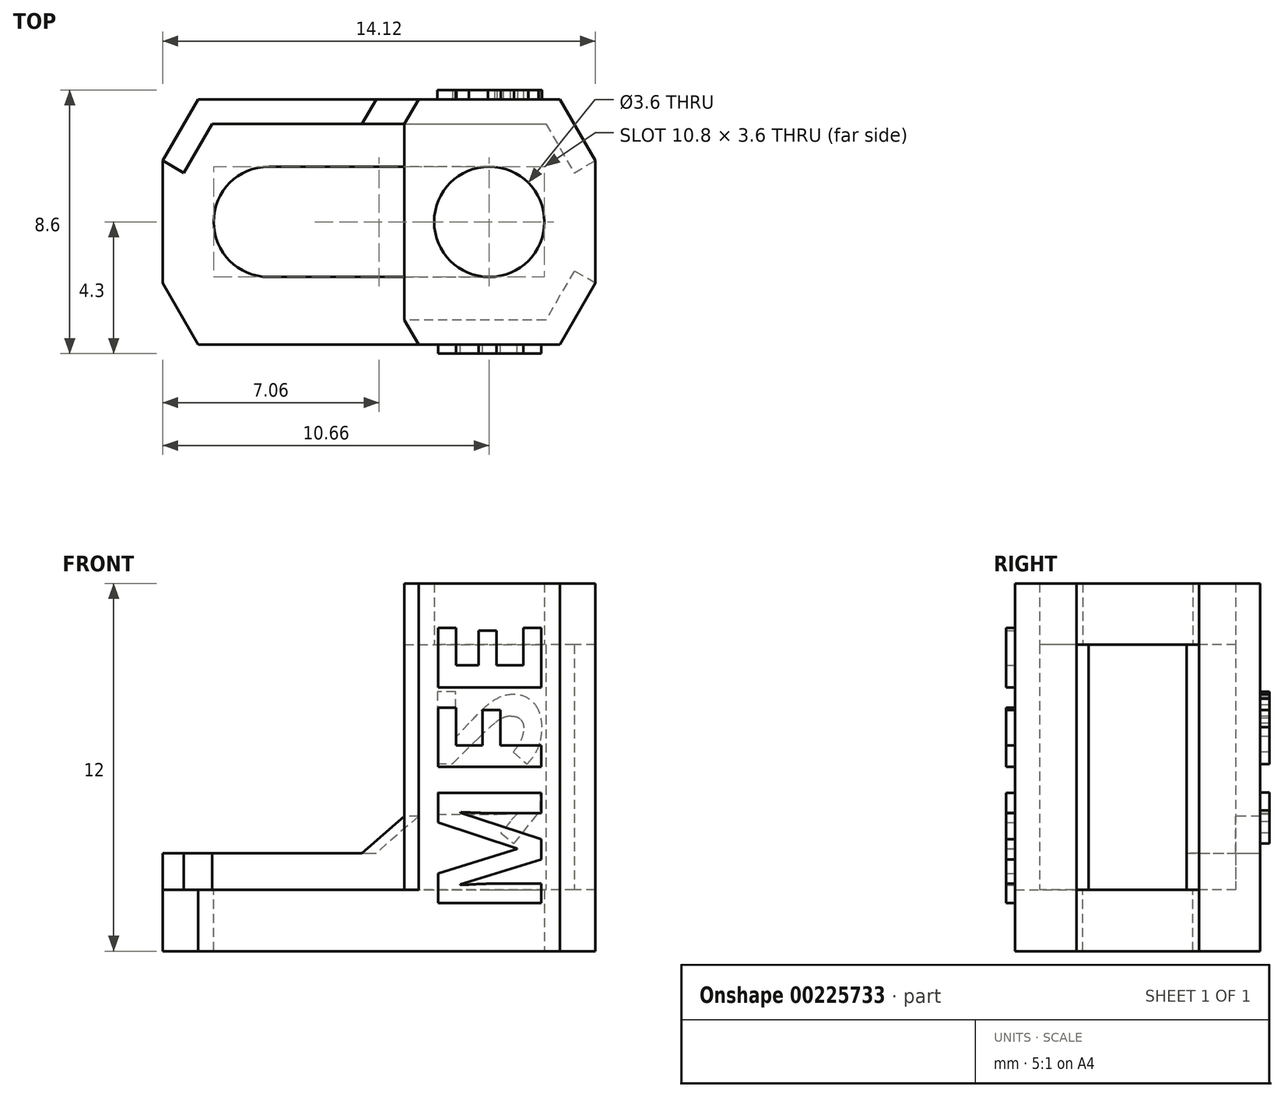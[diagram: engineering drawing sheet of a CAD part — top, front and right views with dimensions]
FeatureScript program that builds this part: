
annotation { "Feature Type Name" : "Feature", "Feature Type Description" : "" }
export const myFeature = defineFeature(function(context is Context, id is Id, definition is map)
    precondition{}
    {
        {
            assignVariable(context, id + "F0", {"name" : "Hex_Nut", "anyValue" : 6.4});
        }
        {
            assignVariable(context, id + "F1", {"name" : "Wall_thick", "anyValue" : 0.8});
        }
        {
            assignVariable(context, id + "F2", {"name" : "Stand_Height", "anyValue" : 12});
        }
        {
            var Q0;
            Q0=qCreatedBy(makeId("Top.planeOp"),FACE);
            var sketch = newSketch(context, id + "F3", { "sketchPlane" : qUnion([Q0])});
            skCircle(sketch, "E0.cCircle", {"center": v(0, 0) * mm, "radius": 4 * mm, "construction": true});
            skLineSegment(sketch, "E0.0", {"start": v(-2.3, 4) * mm, "end": v(2.3, 4) * mm});
            skLineSegment(sketch, "E0.1", {"start": v(2.3, 4) * mm, "end": v(3.46, 2) * mm});
            skLineSegment(sketch, "E0.2", {"start": v(3.46, -2) * mm, "end": v(2.3, -4) * mm});
            skLineSegment(sketch, "E0.3", {"start": v(2.3, -4) * mm, "end": v(-2.3, -4) * mm});
            skLineSegment(sketch, "E0.4", {"start": v(-2.3, -4) * mm, "end": v(-2.77, -3.2) * mm});
            skLineSegment(sketch, "E0.5", {"start": v(-2.77, 3.2) * mm, "end": v(-2.3, 4) * mm});
            skPoint(sketch, "E0.0.midPoint", {"position": v(0, 4) * mm});
            skCircle(sketch, "E1", {"center": v(0, 0) * mm, "radius": 1.8 * mm, "construction": true});
            skLineSegment(sketch, "E2", {"start": v(-2.77, 3.2) * mm, "end": v(-2.77, -3.2) * mm});
            skLineSegment(sketch, "E3", {"start": v(3.46, 2) * mm, "end": v(3.46, -2) * mm});
            skPoint(sketch, "E4.orphan", {"position": v(-4.62, 0) * mm});
            skPoint(sketch, "E5.orphan", {"position": v(4.62, 0) * mm});
            skSolve(sketch);
        }
        {
            var Q0;
            Q0=qCreatedBy(makeId("Top.planeOp"),FACE);
            var sketch = newSketch(context, id + "F4", { "sketchPlane" : qUnion([Q0])});
            skCircle(sketch, "E6.cCircle", {"center": v(0, 0) * mm, "radius": 3.2 * mm, "construction": true});
            skLineSegment(sketch, "E6.0", {"start": v(-5, 3.2) * mm, "end": v(1.85, 3.2) * mm});
            skLineSegment(sketch, "E6.1", {"start": v(1.85, 3.2) * mm, "end": v(2.77, 1.6) * mm});
            skLineSegment(sketch, "E6.2", {"start": v(2.77, -1.6) * mm, "end": v(1.85, -3.2) * mm});
            skLineSegment(sketch, "E6.3", {"start": v(1.85, -3.2) * mm, "end": v(-5, -3.2) * mm});
            skLineSegment(sketch, "E6.4", {"start": v(-1.85, -3.2) * mm, "end": v(-3.7, 0) * mm, "construction": true});
            skLineSegment(sketch, "E6.5", {"start": v(-3.7, 0) * mm, "end": v(-1.85, 3.2) * mm, "construction": true});
            skPoint(sketch, "E6.0.midPoint", {"position": v(0, 3.2) * mm});
            skLineSegment(sketch, "E7", {"start": v(2.77, 1.6) * mm, "end": v(5, 2.89) * mm});
            skLineSegment(sketch, "E8", {"start": v(5, 2.89) * mm, "end": v(5, -2.89) * mm});
            skLineSegment(sketch, "E9", {"start": v(5, -2.89) * mm, "end": v(2.77, -1.6) * mm});
            skLineSegment(sketch, "E10", {"start": v(-5, 3.2) * mm, "end": v(-5, -3.2) * mm});
            skPoint(sketch, "E11.orphan", {"position": v(3.7, 0) * mm});
            skSolve(sketch);
        }
        {
            var Q0;
            Q0=qCreatedBy(makeId("Top.planeOp"),FACE);
            var sketch = newSketch(context, id + "F5", { "sketchPlane" : qUnion([Q0])});
            skCircle(sketch, "E12", {"center": v(0, 0) * mm, "radius": 1.8 * mm});
            skSolve(sketch);
        }
        {
            var Q0;
            Q0=qSketchRegion(id+"F3",true);
            extrude(context, id + "F6", {"entities" : qUnion([Q0]), "endBound" : BoundingType.SYMMETRIC, "depth" : (getVariable(context, 'Stand_Height')) * mm});
        }
        {
            var Q0;
            Q0=qSketchRegion(id+"F4",true);
            extrude(context, id + "F7", {"entities" : qUnion([Q0]), "operationType" : NewBodyOperationType.REMOVE, "endBound" : BoundingType.SYMMETRIC, "depth" : (getVariable(context, 'Stand_Height') - 4) * mm});
        }
        {
            var Q0;
            Q0=qSketchRegion(id+"F5",true);
            extrude(context, id + "F8", {"entities" : qUnion([Q0]), "operationType" : NewBodyOperationType.REMOVE, "endBound" : BoundingType.SYMMETRIC, "depth" : (getVariable(context, 'Stand_Height')) * mm});
        }
        {
            var Q0;
            Q0=qCreatedBy(makeId("Front.planeOp"),FACE);
            var sketch = newSketch(context, id + "F9", { "sketchPlane" : qUnion([Q0])});
            skText(sketch, "E13", { "text": "MFE", "fontName": "OpenSans-Bold.ttf"});
            const initialGuessF9  = {"E13": [0.0017, -0.00486, 0, 1, 0.0034]};
            skSetInitialGuess(sketch, initialGuessF9);
            skSolve(sketch);
        }
        {
            var Q0;
            Q0=qSketchRegion(id+"F9",true);
            extrude(context, id + "F10", {"entities" : qUnion([Q0]), "operationType" : NewBodyOperationType.ADD, "depth" : ((getVariable(context, 'Hex_Nut') / 2) + getVariable(context, 'Wall_thick') + 0.3) * mm, "hasSecondDirection" : true, "secondDirectionOppositeDirection" : false, "secondDirectionDepth" : ((getVariable(context, 'Hex_Nut') / 2) + 0.2) * mm});
        }
        {
            var Q0;
            Q0=makeQuery(id+"F6.opExtrude","SWEPT_FACE",FACE,{"disambiguationData":[OSD([sQuery(id+"F3.wireOp",EDGE,"E0.0")])]});
            var sketch = newSketch(context, id + "F11", { "sketchPlane" : qUnion([Q0])});
            skText(sketch, "E14", { "text": "12", "fontName": "OpenSans-Bold.ttf"});
            const initialGuessF11  = {"E14": [0.0017, -0.00277, 0, 1, 0.0034]};
            skSetInitialGuess(sketch, initialGuessF11);
            skSolve(sketch);
        }
        {
            var Q0;
            Q0=qSketchRegion(id+"F11",true);
            extrude(context, id + "F12", {"entities" : qUnion([Q0]), "operationType" : NewBodyOperationType.ADD, "depth" : 0.3 * mm});
        }
        {
            var Q0;
            Q0=qCreatedBy(makeId("Top.planeOp"),FACE);
            var sketch = newSketch(context, id + "F13", { "sketchPlane" : qUnion([Q0])});
            skLineSegment(sketch, "E15", {"start": v(0, 1.8) * mm, "end": v(-10.64, 1.8) * mm});
            skLineSegment(sketch, "E16", {"start": v(-10.64, 1.8) * mm, "end": v(-10.64, -1.8) * mm});
            skLineSegment(sketch, "E17", {"start": v(-10.64, -1.8) * mm, "end": v(0, -1.8) * mm});
            skLineSegment(sketch, "E18", {"start": v(0, 1.8) * mm, "end": v(0, -1.8) * mm});
            skSolve(sketch);
        }
        {
            var Q0;
            Q0=qSketchRegion(id+"F13",true);
            extrude(context, id + "F14", {"entities" : qUnion([Q0]), "operationType" : NewBodyOperationType.REMOVE, "endBound" : BoundingType.THROUGH_ALL, "oppositeDirection" : true, "depth" : 25 * mm});
        }
        {
            var Q0;
            Q0=qCreatedBy(makeId("Top.planeOp"),FACE);
            var sketch = newSketch(context, id + "F15", { "sketchPlane" : qUnion([Q0])});
            skLineSegment(sketch, "E19", {"start": v(-2.3, 4) * mm, "end": v(-9.5, 4) * mm});
            skLineSegment(sketch, "E20", {"start": v(-9.5, -4) * mm, "end": v(-2.3, -4) * mm});
            skLineSegment(sketch, "E21", {"start": v(-2.3, -4) * mm, "end": v(-2.3, -1.8) * mm});
            skLineSegment(sketch, "E22", {"start": v(-2.3, -1.8) * mm, "end": v(-7.2, -1.8) * mm});
            skLineSegment(sketch, "E23", {"start": v(-2.3, 4) * mm, "end": v(-2.3, 1.8) * mm});
            skLineSegment(sketch, "E24", {"start": v(-2.3, 1.8) * mm, "end": v(-7.2, 1.8) * mm});
            skArc(sketch, "E25", {"start": v(-7.2, 1.8) * mm, "mid": v(-9, 0) * mm, "end": v(-7.2, -1.8) * mm});
            skLineSegment(sketch, "E26", {"start": v(-9.5, 4) * mm, "end": v(-10.66, 2) * mm});
            skLineSegment(sketch, "E27", {"start": v(-10.66, 2) * mm, "end": v(-10.66, -2) * mm});
            skLineSegment(sketch, "E28", {"start": v(-10.66, -2) * mm, "end": v(-9.5, -4) * mm});
            skLineSegment(sketch, "E29", {"start": v(1.8, 0) * mm, "end": v(3.46, 0) * mm, "construction": true});
            skLineSegment(sketch, "E30", {"start": v(-10.66, 0) * mm, "end": v(-9, 0) * mm, "construction": true});
            skSolve(sketch);
        }
        {
            var Q0;
            Q0=qSketchRegion(id+"F15",true);
            var Q1;
            Q1=makeQuery(id+"F6.opExtrude","CAP_FACE",FACE,{"disambiguationData":[OSD([sQuery(id+"F3.wireOp",EDGE,"E0.0"),sQuery(id+"F3.wireOp",EDGE,"E0.1"),sQuery(id+"F3.wireOp",EDGE,"E0.2"),sQuery(id+"F3.wireOp",EDGE,"E0.3"),sQuery(id+"F3.wireOp",EDGE,"E0.4"),sQuery(id+"F3.wireOp",EDGE,"E0.5"),sQuery(id+"F3.wireOp",EDGE,"E2"),sQuery(id+"F3.wireOp",EDGE,"E3")])],"isStart":true});
            var Q2;
            Q2=makeQuery(id+"F7.boolean.opBoolean","COPY",FACE,{"derivedFrom":makeQuery(id+"F7.opExtrude","CAP_FACE",FACE,{"disambiguationData":[OSD([sQuery(id+"F4.wireOp",EDGE,"E6.0"),sQuery(id+"F4.wireOp",EDGE,"E6.1"),sQuery(id+"F4.wireOp",EDGE,"E6.2"),sQuery(id+"F4.wireOp",EDGE,"E6.3"),sQuery(id+"F4.wireOp",EDGE,"E7"),sQuery(id+"F4.wireOp",EDGE,"E8"),sQuery(id+"F4.wireOp",EDGE,"E9"),sQuery(id+"F4.wireOp",EDGE,"E10")])],"isStart":true})});
            extrude(context, id + "F16", {"entities" : qUnion([Q0]), "operationType" : NewBodyOperationType.ADD, "endBound" : BoundingType.UP_TO_SURFACE, "oppositeDirection" : true, "endBoundEntityFace" : qUnion([Q1]), "depth" : 25 * mm, "hasSecondDirection" : true, "secondDirectionBound" : SecondDirectionBoundingType.UP_TO_SURFACE, "secondDirectionOppositeDirection" : true, "secondDirectionBoundEntityFace" : qUnion([Q2]), "secondDirectionDepth" : 25 * mm});
        }
        {
            var Q0;
            Q0=makeQuery(id+"F16.boolean.opBoolean","MERGE",FACE,{"derivedFrom":[makeQuery(id+"F7.boolean.opBoolean","COPY",FACE,{"derivedFrom":makeQuery(id+"F7.opExtrude","CAP_FACE",FACE,{"disambiguationData":[OSD([sQuery(id+"F4.wireOp",EDGE,"E6.0"),sQuery(id+"F4.wireOp",EDGE,"E6.1"),sQuery(id+"F4.wireOp",EDGE,"E6.2"),sQuery(id+"F4.wireOp",EDGE,"E6.3"),sQuery(id+"F4.wireOp",EDGE,"E7"),sQuery(id+"F4.wireOp",EDGE,"E8"),sQuery(id+"F4.wireOp",EDGE,"E9"),sQuery(id+"F4.wireOp",EDGE,"E10")])],"isStart":true})}),makeQuery(id+"F16.opExtrude","CAP_FACE",FACE,{"disambiguationData":[OSD([sQuery(id+"F15.wireOp",EDGE,"E19"),sQuery(id+"F15.wireOp",EDGE,"E20"),sQuery(id+"F15.wireOp",EDGE,"E21"),sQuery(id+"F15.wireOp",EDGE,"E22"),sQuery(id+"F15.wireOp",EDGE,"E23"),sQuery(id+"F15.wireOp",EDGE,"E24"),sQuery(id+"F15.wireOp",EDGE,"E25"),sQuery(id+"F15.wireOp",EDGE,"E26"),sQuery(id+"F15.wireOp",EDGE,"E27"),sQuery(id+"F15.wireOp",EDGE,"E28")])],"isStart":true})]});
            var sketch = newSketch(context, id + "F17", { "sketchPlane" : qUnion([Q0])});
            skLineSegment(sketch, "E31.0", {"start": v(-9.05, 3.2) * mm, "end": v(-2.3, 3.2) * mm});
            skLineSegment(sketch, "E31.1", {"start": v(-9.97, 1.6) * mm, "end": v(-9.05, 3.2) * mm});
            skLineSegment(sketch, "E32", {"start": v(-10.66, 2) * mm, "end": v(-9.97, 1.6) * mm});
            skLineSegment(sketch, "E33", {"start": v(-2.3, 3.2) * mm, "end": v(-2.3, 4) * mm});
            skLineSegment(sketch, "E34.0", {"start": v(-9.5, 4) * mm, "end": v(-2.3, 4) * mm});
            skLineSegment(sketch, "E35.0", {"start": v(-10.66, 2) * mm, "end": v(-9.5, 4) * mm});
            skSolve(sketch);
        }
        {
            var Q0;
            Q0=qSketchRegion(id+"F17",true);
            extrude(context, id + "F18", {"entities" : qUnion([Q0]), "operationType" : NewBodyOperationType.ADD, "depth" : 1.2 * mm});
        }
        {
            var Q0;
            Q0=makeQuery(id+"FBYMjbiBWdrfZ9F_1.1.F18.boolean.opBoolean","INTERSECT",EDGE,{"derivedFrom":[makeQuery(id+"F6.opExtrude","SWEPT_FACE",FACE,{"disambiguationData":[OSD([sQuery(id+"F3.wireOp",EDGE,"E0.4")])]}),makeQuery(id+"FBYMjbiBWdrfZ9F_1.1.F18.opExtrude","CAP_FACE",FACE,{"disambiguationData":[OSD([sQuery(id+"F17.wireOp",EDGE,"E31.0"),sQuery(id+"F17.wireOp",EDGE,"E31.1"),sQuery(id+"F17.wireOp",EDGE,"E32"),sQuery(id+"F17.wireOp",EDGE,"E33"),sQuery(id+"F17.wireOp",EDGE,"E34.0"),sQuery(id+"F17.wireOp",EDGE,"E35.0")])],"isStart":false})]});
            var Q1;
            Q1=makeQuery(id+"F18.boolean.opBoolean","INTERSECT",EDGE,{"derivedFrom":[makeQuery(id+"F6.opExtrude","SWEPT_FACE",FACE,{"disambiguationData":[OSD([sQuery(id+"F3.wireOp",EDGE,"E0.5")])]}),makeQuery(id+"F18.opExtrude","CAP_FACE",FACE,{"disambiguationData":[OSD([sQuery(id+"F17.wireOp",EDGE,"E31.0"),sQuery(id+"F17.wireOp",EDGE,"E31.1"),sQuery(id+"F17.wireOp",EDGE,"E32"),sQuery(id+"F17.wireOp",EDGE,"E33"),sQuery(id+"F17.wireOp",EDGE,"E34.0"),sQuery(id+"F17.wireOp",EDGE,"E35.0")])],"isStart":false})]});
            chamfer(context, id + "F19", {"entities" : qUnion([Q0, Q1]), "width" : 1.2 * mm, "tangentPropagation" : true});
        }
    });
